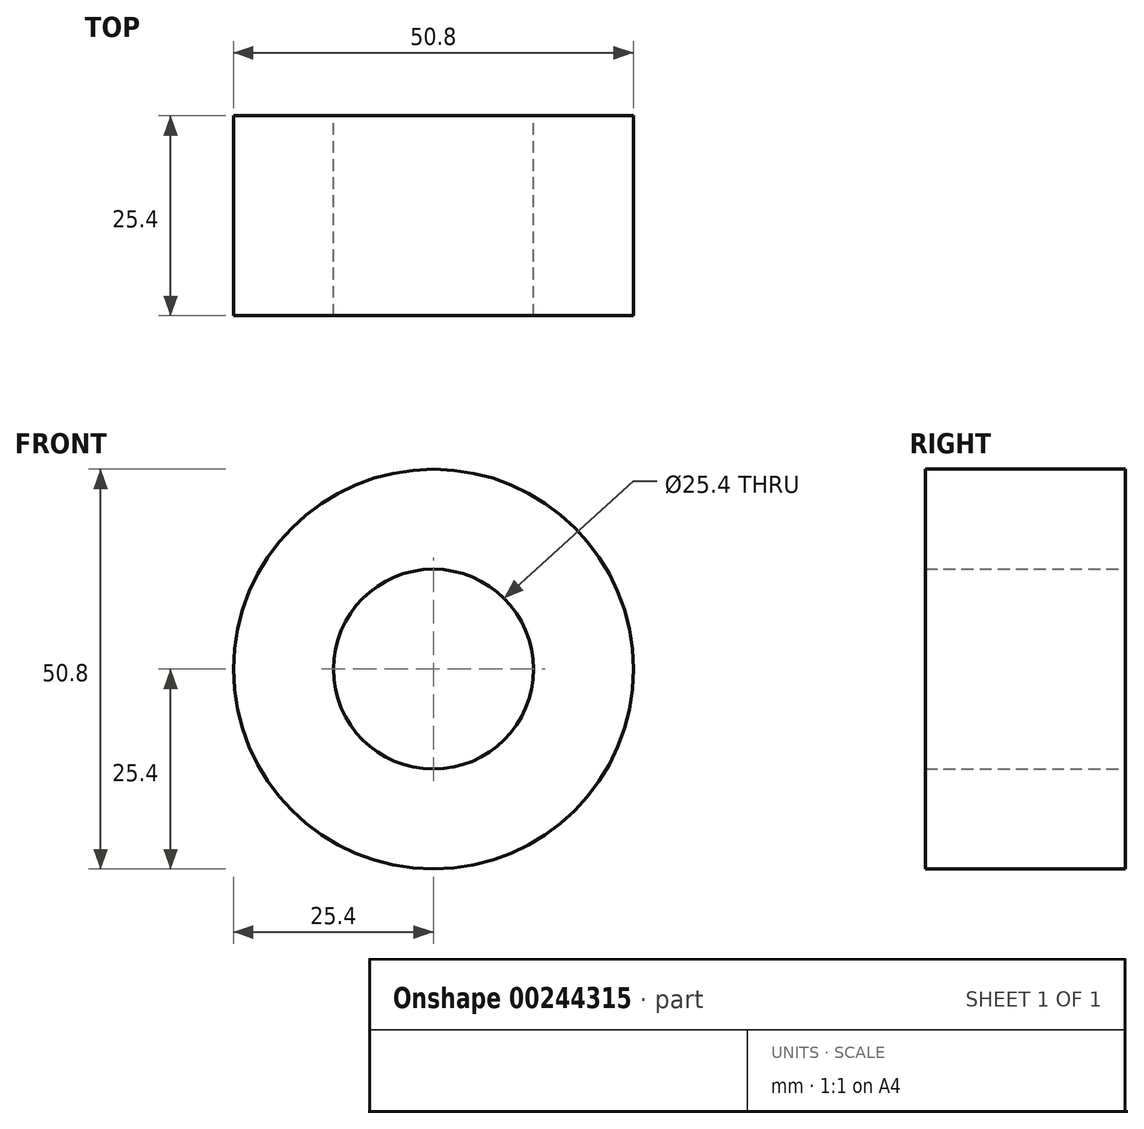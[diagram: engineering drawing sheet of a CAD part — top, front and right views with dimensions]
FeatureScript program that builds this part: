
annotation { "Feature Type Name" : "Feature", "Feature Type Description" : "" }
export const myFeature = defineFeature(function(context is Context, id is Id, definition is map)
    precondition{}
    {
        {
            var Q0;
            Q0=qCreatedBy(makeId("Front.planeOp"),FACE);
            var sketch = newSketch(context, id + "F0", { "sketchPlane" : qUnion([Q0])});
            skCircle(sketch, "E0", {"center": v(0, 0) * mm, "radius": 25.4 * mm});
            skCircle(sketch, "E1", {"center": v(0, 0) * mm, "radius": 12.7 * mm});
            skSolve(sketch);
        }
        {
            var Q0;
            Q0=makeQuery(id+"F0.imprint","IMPRINT",FACE,{"disambiguationData":[TD([[makeQuery(id+"F0.imprint","IMPRINT",EDGE,{"derivedFrom":sQuery(id+"F0.wireOp",EDGE,"E0")}),1.0]])]});
            extrude(context, id + "F1", {"entities" : qUnion([Q0]), "depth" : 25.4 * mm});
        }
    });
